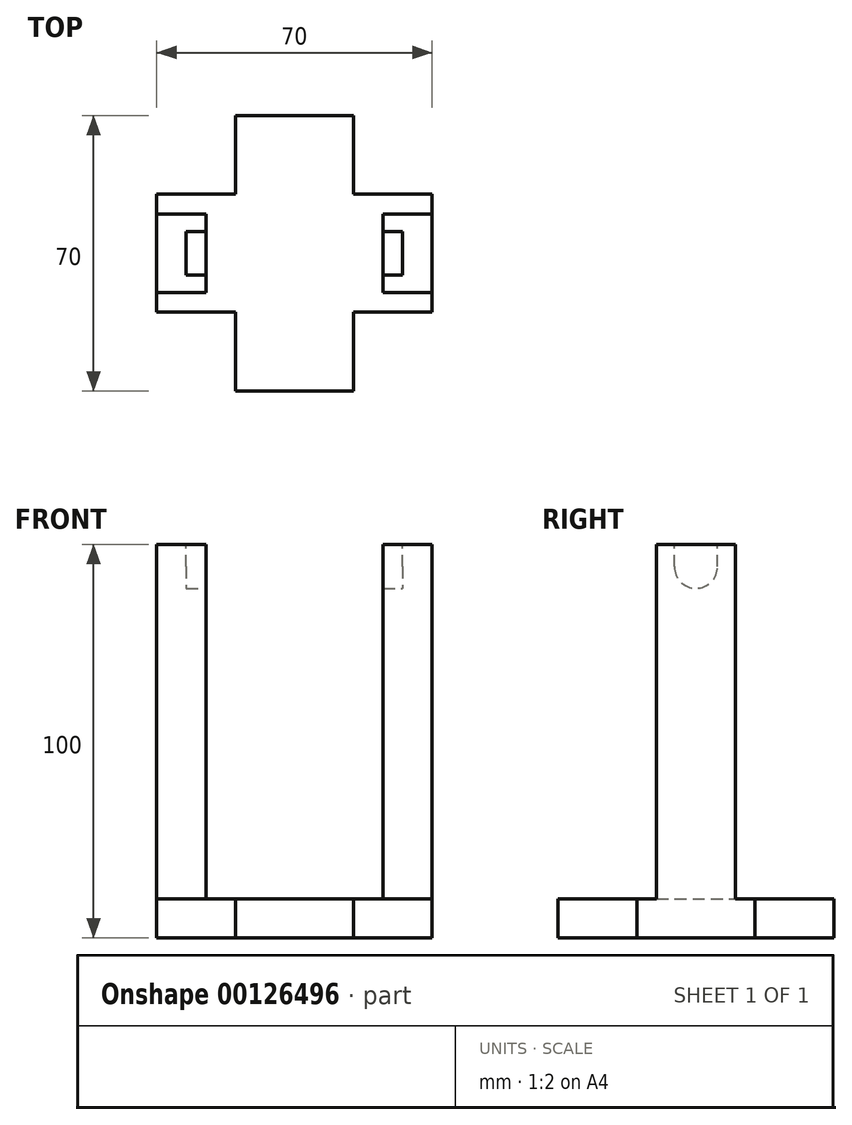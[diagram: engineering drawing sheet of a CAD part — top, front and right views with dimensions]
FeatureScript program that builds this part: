
annotation { "Feature Type Name" : "Feature", "Feature Type Description" : "" }
export const myFeature = defineFeature(function(context is Context, id is Id, definition is map)
    precondition{}
    {
        {
            var Q0;
            Q0=qCreatedBy(makeId("Top.planeOp"),FACE);
            var sketch = newSketch(context, id + "F0", { "sketchPlane" : qUnion([Q0])});
            skLineSegment(sketch, "E0.bottom", {"start": v(35, -15) * mm, "end": v(-35, -15) * mm});
            skLineSegment(sketch, "E0.top", {"start": v(35, 15) * mm, "end": v(-35, 15) * mm});
            skLineSegment(sketch, "E0.left", {"start": v(35, -15) * mm, "end": v(35, 15) * mm});
            skLineSegment(sketch, "E0.right", {"start": v(-35, -15) * mm, "end": v(-35, 15) * mm});
            skPoint(sketch, "E0.middle", {"position": v(0, 0) * mm});
            skLineSegment(sketch, "E1.bottom", {"start": v(15, -35) * mm, "end": v(-15, -35) * mm});
            skLineSegment(sketch, "E1.top", {"start": v(15, 35) * mm, "end": v(-15, 35) * mm});
            skLineSegment(sketch, "E1.left", {"start": v(15, -35) * mm, "end": v(15, 35) * mm});
            skLineSegment(sketch, "E1.right", {"start": v(-15, -35) * mm, "end": v(-15, 35) * mm});
            skSolve(sketch);
        }
        {
            var Q0;
            Q0 = qSketchRegion(id + "F0", true);
            extrude(context, id + "F1", {"entities" : qUnion([Q0]), "depth" : 10 * mm});
        }
        {
            var Q0;
            Q0=qCreatedBy(makeId("Top.planeOp"),FACE);
            var sketch = newSketch(context, id + "F2", { "sketchPlane" : qUnion([Q0])});
            skLineSegment(sketch, "E2.bottom", {"start": v(-35, 10) * mm, "end": v(-22.5, 10) * mm});
            skLineSegment(sketch, "E2.top", {"start": v(-35, -10) * mm, "end": v(-22.5, -10) * mm});
            skLineSegment(sketch, "E2.left", {"start": v(-35, 10) * mm, "end": v(-35, -10) * mm});
            skLineSegment(sketch, "E2.right", {"start": v(-22.5, 10) * mm, "end": v(-22.5, -10) * mm});
            skLineSegment(sketch, "E3.MirrorCS", {"start": v(22.5, 10) * mm, "end": v(22.5, -10) * mm});
            skLineSegment(sketch, "E4.MirrorCS", {"start": v(35, 10) * mm, "end": v(22.5, 10) * mm});
            skLineSegment(sketch, "E5.MirrorCS", {"start": v(35, 10) * mm, "end": v(35, -10) * mm});
            skLineSegment(sketch, "E6.MirrorCS", {"start": v(35, -10) * mm, "end": v(22.5, -10) * mm});
            skSolve(sketch);
        }
        {
            var Q0;
            Q0 = qSketchRegion(id + "F2", true);
            extrude(context, id + "F3", {"entities" : qUnion([Q0]), "operationType" : NewBodyOperationType.ADD, "depth" : 100 * mm});
        }
        {
            var Q0;
            Q0=qCreatedBy(makeId("Right.planeOp"),FACE);
            var sketch = newSketch(context, id + "F4", { "sketchPlane" : qUnion([Q0])});
            skLineSegment(sketch, "E7.0.0", {"start": v(-15, 0) * mm, "end": v(15, 0) * mm, "construction": true});
            skLineSegment(sketch, "E7.0.1", {"start": v(15, 0) * mm, "end": v(15, 100) * mm, "construction": true});
            skLineSegment(sketch, "E7.0.2", {"start": v(15, 100) * mm, "end": v(-15, 100) * mm, "construction": true});
            skLineSegment(sketch, "E7.0.3", {"start": v(-15, 100) * mm, "end": v(-15, 0) * mm, "construction": true});
            skArc(sketch, "E8", {"start": v(-5.5, 94.36) * mm, "mid": v(0, 88.86) * mm, "end": v(5.5, 94.36) * mm});
            skLineSegment(sketch, "E9", {"start": v(5.5, 94.36) * mm, "end": v(5.5, 100) * mm});
            skLineSegment(sketch, "E10", {"start": v(-5.5, 94.36) * mm, "end": v(-5.5, 100) * mm});
            skLineSegment(sketch, "E11", {"start": v(-5.5, 100) * mm, "end": v(5.5, 100) * mm});
            skSolve(sketch);
        }
        {
            var Q0;
            Q0 = qSketchRegion(id + "F4", true);
            extrude(context, id + "F5", {"entities" : qUnion([Q0]), "operationType" : NewBodyOperationType.REMOVE, "endBound" : BoundingType.SYMMETRIC, "oppositeDirection" : true, "depth" : 55 * mm});
        }
    });
